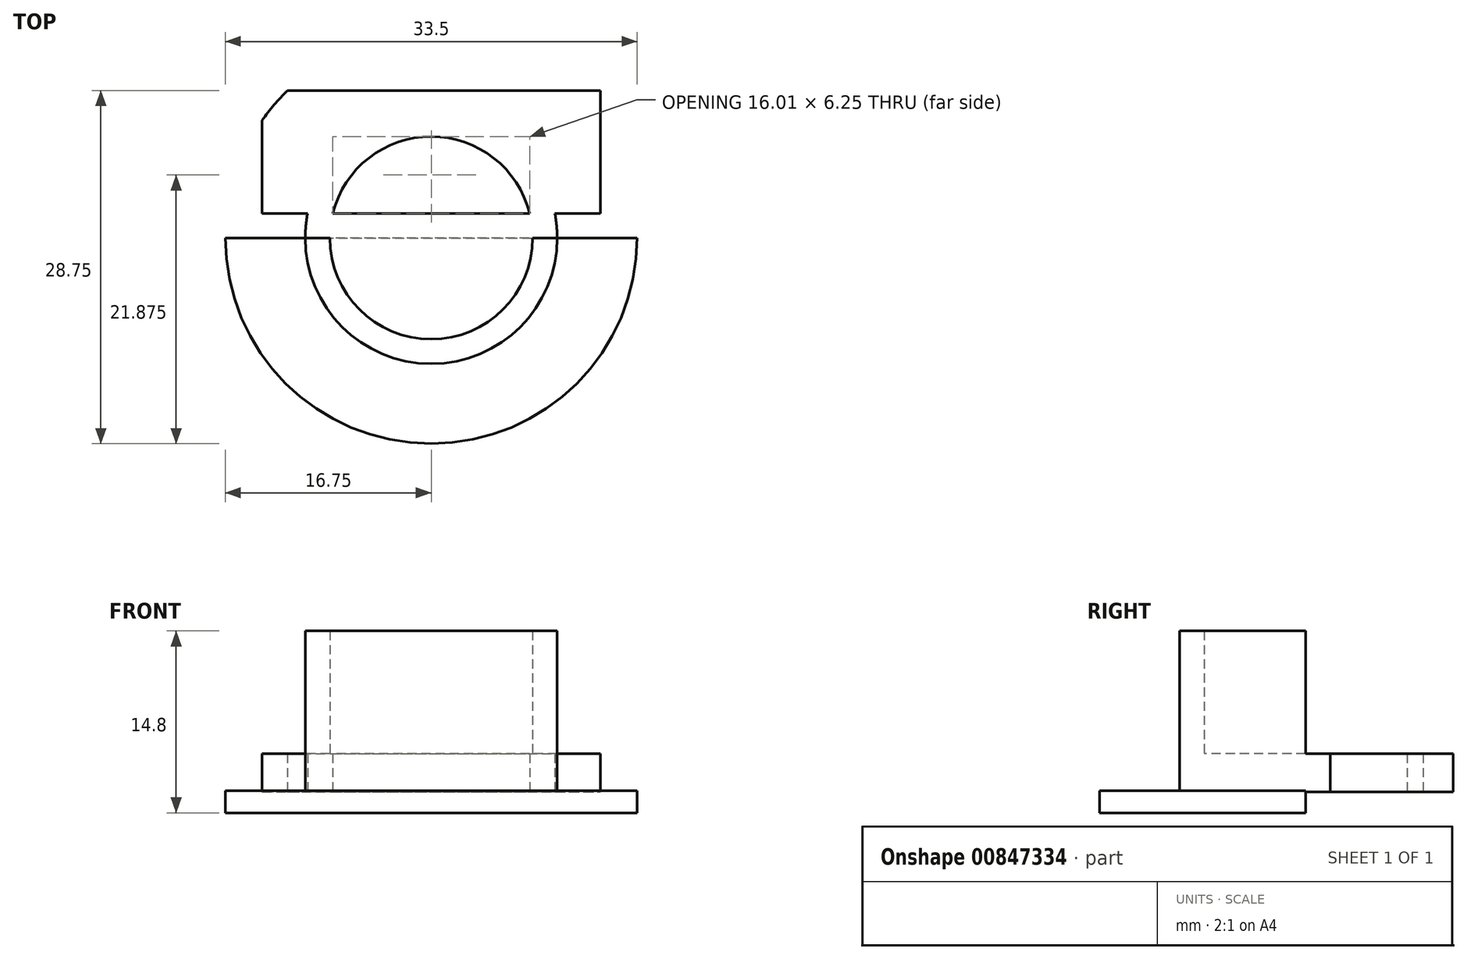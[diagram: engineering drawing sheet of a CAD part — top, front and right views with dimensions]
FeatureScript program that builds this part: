
annotation { "Feature Type Name" : "Feature", "Feature Type Description" : "" }
export const myFeature = defineFeature(function(context is Context, id is Id, definition is map)
    precondition{}
    {
        {
            var Q0;
            Q0=qCreatedBy(makeId("Top.planeOp"),FACE);
            var sketch = newSketch(context, id + "F0", { "sketchPlane" : qUnion([Q0])});
            skCircle(sketch, "E0", {"center": v(0, 0) * mm, "radius": 16.75 * mm});
            skCircle(sketch, "E1", {"center": v(0, 0) * mm, "radius": 10.25 * mm});
            skPoint(sketch, "E2", {"position": v(-16.75, 0) * mm});
            skPoint(sketch, "E3", {"position": v(16.75, 0) * mm});
            skPoint(sketch, "E4", {"position": v(10.25, 0) * mm});
            skPoint(sketch, "E5", {"position": v(-10.25, 0) * mm});
            skLineSegment(sketch, "E6", {"start": v(-16.75, 0) * mm, "end": v(-16.75, 12) * mm});
            skLineSegment(sketch, "E7", {"start": v(-16.75, 12) * mm, "end": v(16.75, 12) * mm});
            skLineSegment(sketch, "E8", {"start": v(16.75, 12) * mm, "end": v(16.75, 0) * mm});
            skLineSegment(sketch, "E9", {"start": v(-16.75, 0) * mm, "end": v(-10.25, 0) * mm});
            skLineSegment(sketch, "E10", {"start": v(10.25, 0) * mm, "end": v(16.75, 0) * mm});
            skLineSegment(sketch, "E11", {"start": v(-10.25, 0) * mm, "end": v(10.25, 0) * mm});
            skLineSegment(sketch, "E12", {"start": v(-13.75, 12) * mm, "end": v(-13.75, 0) * mm});
            skLineSegment(sketch, "E13", {"start": v(13.75, 12) * mm, "end": v(13.75, 0) * mm});
            skCircle(sketch, "E14", {"center": v(0, 0) * mm, "radius": 8.25 * mm});
            skLineSegment(sketch, "E15", {"start": v(-13.75, 2) * mm, "end": v(13.75, 2) * mm});
            skSolve(sketch);
        }
        {
            var Q0;
            {var subQ0=sQuery(id+"F0.wireOp",EDGE,"E9");Q0=makeQuery(id+"F0.imprint","IMPRINT",FACE,{"disambiguationData":[TD([[makeQuery(id+"F0.imprint","IMPRINT",EDGE,{"derivedFrom":subQ0}),-1.0]])]});}
            var Q1;
            {var subQ0=sQuery(id+"F0.wireOp",EDGE,"E11");var subQ4=sQuery(id+"F0.wireOp",EDGE,"E14");var subQ5=makeQuery(id+"F0.imprint","INTERSECT",VERTEX,{"disambiguationData":[OD(0.0)],"derivedFrom":[subQ0,subQ4]});Q1=makeQuery(id+"F0.imprint","IMPRINT",FACE,{"disambiguationData":[TD([[makeQuery(id+"F0.imprint","IMPRINT",EDGE,{"disambiguationData":[TD([[subQ5,-1.0]])],"derivedFrom":subQ4}),-1.0]])]});}
            var Q2;
            {var subQ0=sQuery(id+"F0.wireOp",EDGE,"E14");var subQ1=sQuery(id+"F0.wireOp",EDGE,"E11");var subQ2=makeQuery(id+"F0.imprint","INTERSECT",VERTEX,{"disambiguationData":[OD(0.0)],"derivedFrom":[subQ1,subQ0]});Q2=makeQuery(id+"F0.imprint","IMPRINT",FACE,{"disambiguationData":[TD([[makeQuery(id+"F0.imprint","IMPRINT",EDGE,{"disambiguationData":[TD([[subQ2,-1.0]])],"derivedFrom":subQ1}),-1.0]])]});}
            var Q3;
            {var subQ0=sQuery(id+"F0.wireOp",EDGE,"E11");var subQ4=sQuery(id+"F0.wireOp",EDGE,"E14");var subQ5=makeQuery(id+"F0.imprint","INTERSECT",VERTEX,{"disambiguationData":[OD(0.0)],"derivedFrom":[subQ0,subQ4]});Q3=makeQuery(id+"F0.imprint","IMPRINT",FACE,{"disambiguationData":[TD([[makeQuery(id+"F0.imprint","IMPRINT",EDGE,{"disambiguationData":[TD([[subQ5,-1.0]])],"derivedFrom":subQ4}),-1.0]])]});}
            extrude(context, id + "F1", {"entities" : qUnion([Q0, Q1, Q2, Q3]), "oppositeDirection" : true, "depth" : 1.8 * mm, "offsetDistance" : 25 * mm});
        }
        {
            var Q0;
            {var subQ0=sQuery(id+"F0.wireOp",EDGE,"E13");var subQ1=sQuery(id+"F0.wireOp",EDGE,"E0");var subQ2=makeQuery(id+"F0.imprint","INTERSECT",VERTEX,{"derivedFrom":[subQ1,subQ0]});Q0=makeQuery(id+"F0.imprint","IMPRINT",FACE,{"disambiguationData":[TD([[makeQuery(id+"F0.imprint","IMPRINT",EDGE,{"disambiguationData":[TD([[subQ2,-1.0]])],"derivedFrom":subQ1}),-1.0]])]});}
            var Q1;
            {var subQ0=sQuery(id+"F0.wireOp",EDGE,"E11");Q1=makeQuery(id+"F0.imprint","IMPRINT",FACE,{"disambiguationData":[TD([[makeQuery(id+"F0.imprint","IMPRINT",EDGE,{"derivedFrom":subQ0}),1.0]])]});}
            var Q2;
            {var subQ4=sQuery(id+"F0.wireOp",EDGE,"E13");var subQ10=sQuery(id+"F0.wireOp",EDGE,"E0");var subQ11=makeQuery(id+"F0.imprint","INTERSECT",VERTEX,{"derivedFrom":[subQ10,subQ4]});Q2=makeQuery(id+"F0.imprint","IMPRINT",FACE,{"disambiguationData":[TD([[makeQuery(id+"F0.imprint","IMPRINT",EDGE,{"disambiguationData":[TD([[subQ11,-1.0]])],"derivedFrom":subQ10}),1.0]])]});}
            var Q3;
            {var subQ0=sQuery(id+"F0.wireOp",EDGE,"E14");var subQ1=sQuery(id+"F0.wireOp",EDGE,"E11");var subQ2=makeQuery(id+"F0.imprint","INTERSECT",VERTEX,{"disambiguationData":[OD(0.0)],"derivedFrom":[subQ1,subQ0]});Q3=makeQuery(id+"F0.imprint","IMPRINT",FACE,{"disambiguationData":[TD([[makeQuery(id+"F0.imprint","IMPRINT",EDGE,{"disambiguationData":[TD([[subQ2,-1.0]])],"derivedFrom":subQ1}),1.0]])]});}
            var Q4;
            {var subQ0=sQuery(id+"F0.wireOp",EDGE,"E14");var subQ1=sQuery(id+"F0.wireOp",EDGE,"E11");var subQ2=makeQuery(id+"F0.imprint","INTERSECT",VERTEX,{"disambiguationData":[OD(0.0)],"derivedFrom":[subQ1,subQ0]});Q4=makeQuery(id+"F0.imprint","IMPRINT",FACE,{"disambiguationData":[TD([[makeQuery(id+"F0.imprint","IMPRINT",EDGE,{"disambiguationData":[TD([[subQ2,-1.0]])],"derivedFrom":subQ1}),-1.0]])]});}
            var Q5;
            {var subQ0=sQuery(id+"F0.wireOp",EDGE,"E11");var subQ4=sQuery(id+"F0.wireOp",EDGE,"E14");var subQ5=makeQuery(id+"F0.imprint","INTERSECT",VERTEX,{"disambiguationData":[OD(0.0)],"derivedFrom":[subQ0,subQ4]});Q5=makeQuery(id+"F0.imprint","IMPRINT",FACE,{"disambiguationData":[TD([[makeQuery(id+"F0.imprint","IMPRINT",EDGE,{"disambiguationData":[TD([[subQ5,-1.0]])],"derivedFrom":subQ4}),-1.0]])]});}
            var Q6;
            {var subQ0=sQuery(id+"F0.wireOp",EDGE,"E11");var subQ4=sQuery(id+"F0.wireOp",EDGE,"E14");var subQ5=makeQuery(id+"F0.imprint","INTERSECT",VERTEX,{"disambiguationData":[OD(0.0)],"derivedFrom":[subQ0,subQ4]});Q6=makeQuery(id+"F0.imprint","IMPRINT",FACE,{"disambiguationData":[TD([[makeQuery(id+"F0.imprint","IMPRINT",EDGE,{"disambiguationData":[TD([[subQ5,-1.0]])],"derivedFrom":subQ4}),-1.0]])]});}
            var Q7;
            {var subQ0=sQuery(id+"F0.wireOp",EDGE,"E14");var subQ1=sQuery(id+"F0.wireOp",EDGE,"E11");var subQ2=makeQuery(id+"F0.imprint","INTERSECT",VERTEX,{"disambiguationData":[OD(0.0)],"derivedFrom":[subQ1,subQ0]});Q7=makeQuery(id+"F0.imprint","IMPRINT",FACE,{"disambiguationData":[TD([[makeQuery(id+"F0.imprint","IMPRINT",EDGE,{"disambiguationData":[TD([[subQ2,-1.0]])],"derivedFrom":subQ1}),-1.0]])]});}
            var Q8;
            {var subQ0=sQuery(id+"F0.wireOp",EDGE,"E15");var subQ1=sQuery(id+"F0.wireOp",EDGE,"E1");var subQ2=makeQuery(id+"F0.imprint","INTERSECT",VERTEX,{"disambiguationData":[OD(0.0)],"derivedFrom":[subQ1,subQ0]});Q8=makeQuery(id+"F0.imprint","IMPRINT",FACE,{"disambiguationData":[TD([[makeQuery(id+"F0.imprint","IMPRINT",EDGE,{"disambiguationData":[TD([[subQ2,-1.0]])],"derivedFrom":subQ1}),1.0]])]});}
            var Q9;
            {var subQ0=sQuery(id+"F0.wireOp",EDGE,"E15");var subQ1=sQuery(id+"F0.wireOp",EDGE,"E14");var subQ2=makeQuery(id+"F0.imprint","INTERSECT",VERTEX,{"disambiguationData":[OD(0.0)],"derivedFrom":[subQ1,subQ0]});Q9=makeQuery(id+"F0.imprint","IMPRINT",FACE,{"disambiguationData":[TD([[makeQuery(id+"F0.imprint","IMPRINT",EDGE,{"disambiguationData":[TD([[subQ2,-1.0]])],"derivedFrom":subQ1}),1.0]])]});}
            var Q10;
            {var subQ0=sQuery(id+"F0.wireOp",EDGE,"E7");var subQ1=sQuery(id+"F0.wireOp",EDGE,"E0");var subQ2=makeQuery(id+"F0.imprint","INTERSECT",VERTEX,{"disambiguationData":[OD(1.0)],"derivedFrom":[subQ1,subQ0]});Q10=makeQuery(id+"F0.imprint","IMPRINT",FACE,{"disambiguationData":[TD([[makeQuery(id+"F0.imprint","IMPRINT",EDGE,{"disambiguationData":[TD([[subQ2,-1.0]])],"derivedFrom":subQ1}),-1.0]])]});}
            extrude(context, id + "F2", {"entities" : qUnion([Q0, Q1, Q2, Q3, Q4, Q5, Q6, Q7, Q8, Q9, Q10]), "operationType" : NewBodyOperationType.ADD, "depth" : 3 * mm, "offsetDistance" : 25 * mm, "hasSecondDirection" : true, "secondDirectionOppositeDirection" : true, "secondDirectionDepth" : .1 * mm});
        }
        {
            var Q0;
            {var subQ0=sQuery(id+"F0.wireOp",EDGE,"E11");var subQ4=sQuery(id+"F0.wireOp",EDGE,"E14");var subQ5=makeQuery(id+"F0.imprint","INTERSECT",VERTEX,{"disambiguationData":[OD(0.0)],"derivedFrom":[subQ0,subQ4]});Q0=makeQuery(id+"F0.imprint","IMPRINT",FACE,{"disambiguationData":[TD([[makeQuery(id+"F0.imprint","IMPRINT",EDGE,{"disambiguationData":[TD([[subQ5,-1.0]])],"derivedFrom":subQ4}),-1.0]])]});}
            extrude(context, id + "F3", {"entities" : qUnion([Q0]), "operationType" : NewBodyOperationType.ADD, "depth" : 13 * mm, "offsetDistance" : 25 * mm, "hasSecondDirection" : true, "secondDirectionOppositeDirection" : true, "secondDirectionDepth" : 1.7 * mm});
        }
    });
